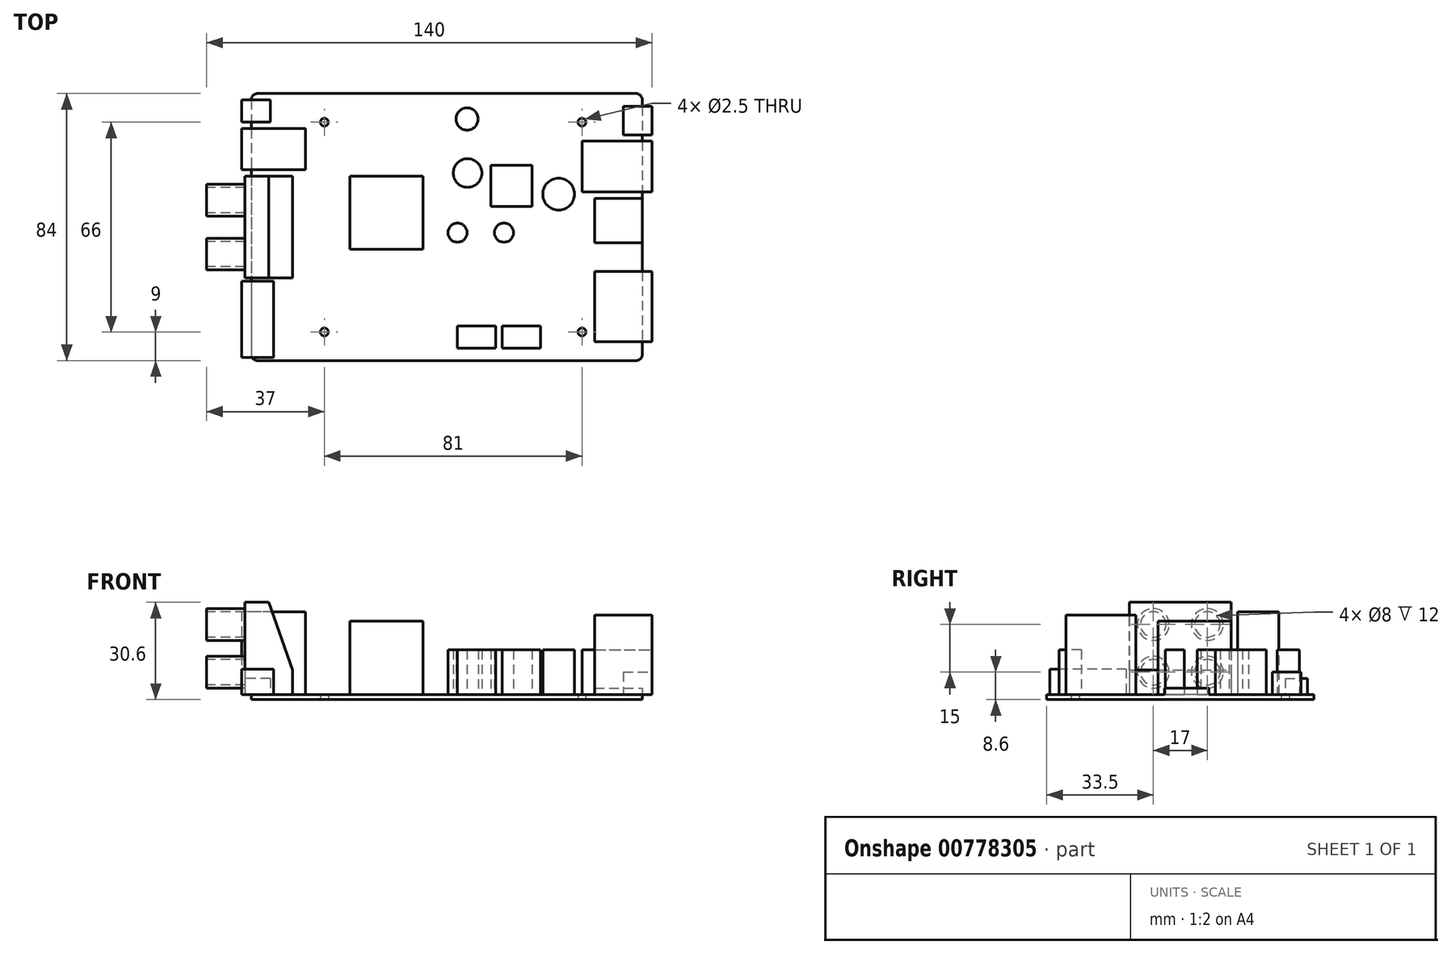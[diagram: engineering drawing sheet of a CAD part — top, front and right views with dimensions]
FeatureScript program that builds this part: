
annotation { "Feature Type Name" : "Feature", "Feature Type Description" : "" }
export const myFeature = defineFeature(function(context is Context, id is Id, definition is map)
    precondition{}
    {
        {
            var Q0;
            Q0=qCreatedBy(makeId("Top.planeOp"),FACE);
            var sketch = newSketch(context, id + "F0", { "sketchPlane" : qUnion([Q0])});
            skLineSegment(sketch, "E0.bottom", {"start": v(-40.5, 33) * mm, "end": v(40.5, 33) * mm, "construction": true});
            skLineSegment(sketch, "E0.top", {"start": v(-40.5, -33) * mm, "end": v(40.5, -33) * mm, "construction": true});
            skLineSegment(sketch, "E0.left", {"start": v(-40.5, 33) * mm, "end": v(-40.5, -33) * mm, "construction": true});
            skLineSegment(sketch, "E0.right", {"start": v(40.5, 33) * mm, "end": v(40.5, -33) * mm, "construction": true});
            skPoint(sketch, "E0.middle", {"position": v(0, 0) * mm});
            skCircle(sketch, "E1", {"center": v(-40.5, 33) * mm, "radius": 1.25 * mm});
            skCircle(sketch, "E2.0.1.0", {"center": v(-40.5, -33) * mm, "radius": 1.25 * mm});
            skCircle(sketch, "E2.1.0.0", {"center": v(40.5, 33) * mm, "radius": 1.25 * mm});
            skCircle(sketch, "E2.1.1.0", {"center": v(40.5, -33) * mm, "radius": 1.25 * mm});
            skLineSegment(sketch, "E3.bottom", {"start": v(-61.5, 42) * mm, "end": v(57.5, 42) * mm});
            skLineSegment(sketch, "E3.top", {"start": v(-61.5, -42) * mm, "end": v(57.5, -42) * mm});
            skLineSegment(sketch, "E3.left", {"start": v(-63.5, 40) * mm, "end": v(-63.5, -40) * mm});
            skLineSegment(sketch, "E3.right", {"start": v(59.5, 40) * mm, "end": v(59.5, -40) * mm});
            skPoint(sketch, "E3.middle", {"position": v(-2, 0) * mm});
            skPoint(sketch, "E4.visualSharp", {"position": v(-63.5, 42) * mm});
            skArc(sketch, "E4.filletArc", {"start": v(-61.5, 42) * mm, "mid": v(-62.91, 41.41) * mm, "end": v(-63.5, 40) * mm});
            skPoint(sketch, "E5.visualSharp", {"position": v(59.5, 42) * mm});
            skArc(sketch, "E5.filletArc", {"start": v(59.5, 40) * mm, "mid": v(58.91, 41.41) * mm, "end": v(57.5, 42) * mm});
            skPoint(sketch, "E6.visualSharp", {"position": v(59.5, -42) * mm});
            skArc(sketch, "E6.filletArc", {"start": v(57.5, -42) * mm, "mid": v(58.91, -41.41) * mm, "end": v(59.5, -40) * mm});
            skPoint(sketch, "E7.visualSharp", {"position": v(-63.5, -42) * mm});
            skArc(sketch, "E7.filletArc", {"start": v(-63.5, -40) * mm, "mid": v(-62.91, -41.41) * mm, "end": v(-61.5, -42) * mm});
            skSolve(sketch);
        }
        {
            var Q0;
            Q0=makeQuery(id+"F0.imprint","IMPRINT",FACE,{"disambiguationData":[TD([[makeQuery(id+"F0.imprint","IMPRINT",EDGE,{"derivedFrom":sQuery(id+"F0.wireOp",EDGE,"E1")}),-1.0]])]});
            extrude(context, id + "F1", {"entities" : qUnion([Q0]), "depth" : 1.6 * mm, "offsetDistance" : 25 * mm});
        }
        {
            var Q0;
            Q0=makeQuery(id+"F1.opExtrude","CAP_FACE",FACE,{"disambiguationData":[OSD([sQuery(id+"F0.wireOp",EDGE,"E1"),sQuery(id+"F0.wireOp",EDGE,"E2.0.1.0"),sQuery(id+"F0.wireOp",EDGE,"E2.1.0.0"),sQuery(id+"F0.wireOp",EDGE,"E2.1.1.0"),sQuery(id+"F0.wireOp",EDGE,"E3.bottom"),sQuery(id+"F0.wireOp",EDGE,"E3.top"),sQuery(id+"F0.wireOp",EDGE,"E3.left"),sQuery(id+"F0.wireOp",EDGE,"E3.right"),sQuery(id+"F0.wireOp",EDGE,"E4.filletArc"),sQuery(id+"F0.wireOp",EDGE,"E5.filletArc"),sQuery(id+"F0.wireOp",EDGE,"E6.filletArc"),sQuery(id+"F0.wireOp",EDGE,"E7.filletArc")])],"isStart":false});
            var sketch = newSketch(context, id + "F2", { "sketchPlane" : qUnion([Q0])});
            skLineSegment(sketch, "E8.bottom", {"start": v(-57.5, 33) * mm, "end": v(-66.5, 33) * mm});
            skLineSegment(sketch, "E8.top", {"start": v(-57.5, 40) * mm, "end": v(-66.5, 40) * mm});
            skLineSegment(sketch, "E8.left", {"start": v(-57.5, 33) * mm, "end": v(-57.5, 40) * mm});
            skLineSegment(sketch, "E8.right", {"start": v(-66.5, 33) * mm, "end": v(-66.5, 40) * mm});
            skPoint(sketch, "E8.middle", {"position": v(-62, 36.5) * mm});
            skLineSegment(sketch, "E9.bottom", {"start": v(-46.5, 18) * mm, "end": v(-66.5, 18) * mm});
            skLineSegment(sketch, "E9.top", {"start": v(-46.5, 31) * mm, "end": v(-66.5, 31) * mm});
            skLineSegment(sketch, "E9.left", {"start": v(-46.5, 18) * mm, "end": v(-46.5, 31) * mm});
            skLineSegment(sketch, "E9.right", {"start": v(-66.5, 18) * mm, "end": v(-66.5, 31) * mm});
            skPoint(sketch, "E9.middle", {"position": v(-56.5, 24.5) * mm});
            skLineSegment(sketch, "E10.bottom", {"start": v(-77.5, 16) * mm, "end": v(-50.5, 16) * mm});
            skLineSegment(sketch, "E10.top", {"start": v(-77.5, 0) * mm, "end": v(-50.5, 0) * mm});
            skLineSegment(sketch, "E10.left", {"start": v(-77.5, 16) * mm, "end": v(-77.5, 0) * mm});
            skLineSegment(sketch, "E10.right", {"start": v(-50.5, 16) * mm, "end": v(-50.5, 0) * mm});
            skPoint(sketch, "E10.middle", {"position": v(-64, 8) * mm});
            skLineSegment(sketch, "E11.bottom", {"start": v(-66.5, -17) * mm, "end": v(-56.5, -17) * mm});
            skLineSegment(sketch, "E11.top", {"start": v(-66.5, -41) * mm, "end": v(-56.5, -41) * mm});
            skLineSegment(sketch, "E11.left", {"start": v(-66.5, -17) * mm, "end": v(-66.5, -41) * mm});
            skLineSegment(sketch, "E11.right", {"start": v(-56.5, -17) * mm, "end": v(-56.5, -41) * mm});
            skPoint(sketch, "E11.middle", {"position": v(-61.5, -29) * mm});
            skLineSegment(sketch, "E12.bottom", {"start": v(53.5, 38) * mm, "end": v(62.5, 38) * mm});
            skLineSegment(sketch, "E12.top", {"start": v(53.5, 29) * mm, "end": v(62.5, 29) * mm});
            skLineSegment(sketch, "E12.left", {"start": v(53.5, 38) * mm, "end": v(53.5, 29) * mm});
            skLineSegment(sketch, "E12.right", {"start": v(62.5, 38) * mm, "end": v(62.5, 29) * mm});
            skPoint(sketch, "E12.middle", {"position": v(58, 33.5) * mm});
            skLineSegment(sketch, "E13.bottom", {"start": v(40.5, 27) * mm, "end": v(62.5, 27) * mm});
            skLineSegment(sketch, "E13.top", {"start": v(40.5, 11) * mm, "end": v(62.5, 11) * mm});
            skLineSegment(sketch, "E13.left", {"start": v(40.5, 27) * mm, "end": v(40.5, 11) * mm});
            skLineSegment(sketch, "E13.right", {"start": v(62.5, 27) * mm, "end": v(62.5, 11) * mm});
            skPoint(sketch, "E13.middle", {"position": v(51.5, 19) * mm});
            skLineSegment(sketch, "E14.bottom", {"start": v(44.5, 9) * mm, "end": v(59.5, 9) * mm});
            skLineSegment(sketch, "E14.top", {"start": v(44.5, -5) * mm, "end": v(59.5, -5) * mm});
            skLineSegment(sketch, "E14.left", {"start": v(44.5, 9) * mm, "end": v(44.5, -5) * mm});
            skLineSegment(sketch, "E14.right", {"start": v(59.5, 9) * mm, "end": v(59.5, -5) * mm});
            skPoint(sketch, "E14.middle", {"position": v(52, 2) * mm});
            skLineSegment(sketch, "E15.bottom", {"start": v(44.5, -14) * mm, "end": v(62.5, -14) * mm});
            skLineSegment(sketch, "E15.top", {"start": v(44.5, -36) * mm, "end": v(62.5, -36) * mm});
            skLineSegment(sketch, "E15.left", {"start": v(44.5, -14) * mm, "end": v(44.5, -36) * mm});
            skLineSegment(sketch, "E15.right", {"start": v(62.5, -14) * mm, "end": v(62.5, -36) * mm});
            skPoint(sketch, "E15.middle", {"position": v(53.5, -25) * mm});
            skLineSegment(sketch, "E16.MirrorCS", {"start": v(-50.5, -16) * mm, "end": v(-50.5, 0) * mm});
            skLineSegment(sketch, "E17.MirrorCS", {"start": v(-77.5, -16) * mm, "end": v(-77.5, 0) * mm});
            skLineSegment(sketch, "E18.MirrorCS", {"start": v(-77.5, -16) * mm, "end": v(-50.5, -16) * mm});
            skLineSegment(sketch, "E19.bottom", {"start": v(-32.5, 16) * mm, "end": v(-9.5, 16) * mm});
            skLineSegment(sketch, "E19.top", {"start": v(-32.5, -7) * mm, "end": v(-9.5, -7) * mm});
            skLineSegment(sketch, "E19.left", {"start": v(-32.5, 16) * mm, "end": v(-32.5, -7) * mm});
            skLineSegment(sketch, "E19.right", {"start": v(-9.5, 16) * mm, "end": v(-9.5, -7) * mm});
            skPoint(sketch, "E19.middle", {"position": v(-21, 4.5) * mm});
            skCircle(sketch, "E20", {"center": v(4.37, 34) * mm, "radius": 3.5 * mm});
            skCircle(sketch, "E21", {"center": v(4.52, 17) * mm, "radius": 4.5 * mm});
            skCircle(sketch, "E22", {"center": v(1.37, -1.76) * mm, "radius": 3 * mm});
            skCircle(sketch, "E23", {"center": v(15.98, -1.76) * mm, "radius": 3 * mm});
            skLineSegment(sketch, "E24.bottom", {"start": v(11.84, 19.5) * mm, "end": v(24.84, 19.5) * mm});
            skLineSegment(sketch, "E24.top", {"start": v(11.84, 6.5) * mm, "end": v(24.84, 6.5) * mm});
            skLineSegment(sketch, "E24.left", {"start": v(11.84, 19.5) * mm, "end": v(11.84, 6.5) * mm});
            skLineSegment(sketch, "E24.right", {"start": v(24.84, 19.5) * mm, "end": v(24.84, 6.5) * mm});
            skPoint(sketch, "E24.middle", {"position": v(18.34, 13) * mm});
            skCircle(sketch, "E25", {"center": v(33.18, 10.36) * mm, "radius": 5 * mm});
            skLineSegment(sketch, "E26.bottom", {"start": v(1.37, -31.15) * mm, "end": v(13.37, -31.15) * mm});
            skLineSegment(sketch, "E26.top", {"start": v(1.37, -38.15) * mm, "end": v(13.37, -38.15) * mm});
            skLineSegment(sketch, "E26.left", {"start": v(1.37, -31.15) * mm, "end": v(1.37, -38.15) * mm});
            skLineSegment(sketch, "E26.right", {"start": v(13.37, -31.15) * mm, "end": v(13.37, -38.15) * mm});
            skLineSegment(sketch, "E27.bottom", {"start": v(15.47, -31.15) * mm, "end": v(27.47, -31.15) * mm});
            skLineSegment(sketch, "E27.top", {"start": v(15.47, -38.15) * mm, "end": v(27.47, -38.15) * mm});
            skLineSegment(sketch, "E27.left", {"start": v(15.47, -31.15) * mm, "end": v(15.47, -38.15) * mm});
            skLineSegment(sketch, "E27.right", {"start": v(27.47, -31.15) * mm, "end": v(27.47, -38.15) * mm});
            skSolve(sketch);
        }
        {
            var Q0;
            {var subQ0=sQuery(id+"F2.wireOp",EDGE,"E8.right");Q0=makeQuery(id+"F2.imprint","IMPRINT",FACE,{"disambiguationData":[TD([[makeQuery(id+"F2.imprint","IMPRINT",EDGE,{"derivedFrom":subQ0}),-1.0]])]});}
            var Q1;
            {var subQ0=sQuery(id+"F2.wireOp",EDGE,"E8.left");Q1=makeQuery(id+"F2.imprint","IMPRINT",FACE,{"disambiguationData":[TD([[makeQuery(id+"F2.imprint","IMPRINT",EDGE,{"derivedFrom":subQ0}),1.0]])]});}
            extrude(context, id + "F3", {"entities" : qUnion([Q0, Q1]), "operationType" : NewBodyOperationType.ADD, "depth" : 5 * mm, "offsetDistance" : 25 * mm});
        }
        {
            var Q0;
            {var subQ5=sQuery(id+"F2.wireOp",EDGE,"E11.right");Q0=makeQuery(id+"F2.imprint","IMPRINT",FACE,{"disambiguationData":[TD([[makeQuery(id+"F2.imprint","IMPRINT",EDGE,{"derivedFrom":subQ5}),-1.0]])]});}
            var Q1;
            {var subQ5=sQuery(id+"F2.wireOp",EDGE,"E11.left");Q1=makeQuery(id+"F2.imprint","IMPRINT",FACE,{"disambiguationData":[TD([[makeQuery(id+"F2.imprint","IMPRINT",EDGE,{"derivedFrom":subQ5}),1.0]])]});}
            extrude(context, id + "F4", {"entities" : qUnion([Q0, Q1]), "operationType" : NewBodyOperationType.ADD, "depth" : 8 * mm, "offsetDistance" : 25 * mm});
        }
        {
            var Q0;
            {var subQ0=sQuery(id+"F2.wireOp",EDGE,"E10.left");Q0=makeQuery(id+"F2.imprint","IMPRINT",FACE,{"disambiguationData":[TD([[makeQuery(id+"F2.imprint","IMPRINT",EDGE,{"derivedFrom":subQ0}),1.0]])]});}
            var Q1;
            {var subQ0=sQuery(id+"F2.wireOp",EDGE,"E10.right");Q1=makeQuery(id+"F2.imprint","IMPRINT",FACE,{"disambiguationData":[TD([[makeQuery(id+"F2.imprint","IMPRINT",EDGE,{"derivedFrom":subQ0}),-1.0]])]});}
            var Q2;
            {var subQ0=sQuery(id+"F2.wireOp",EDGE,"E17.MirrorCS");Q2=makeQuery(id+"F2.imprint","IMPRINT",FACE,{"disambiguationData":[TD([[makeQuery(id+"F2.imprint","IMPRINT",EDGE,{"derivedFrom":subQ0}),-1.0]])]});}
            var Q3;
            {var subQ0=sQuery(id+"F2.wireOp",EDGE,"E16.MirrorCS");Q3=makeQuery(id+"F2.imprint","IMPRINT",FACE,{"disambiguationData":[TD([[makeQuery(id+"F2.imprint","IMPRINT",EDGE,{"derivedFrom":subQ0}),1.0]])]});}
            extrude(context, id + "F5", {"entities" : qUnion([Q0, Q1, Q2, Q3]), "operationType" : NewBodyOperationType.ADD, "depth" : 29 * mm, "offsetDistance" : 25 * mm});
        }
        {
            var Q0;
            Q0=makeQuery(id+"F5.opExtrude","SWEPT_FACE",FACE,{"disambiguationData":[OSD([sQuery(id+"F2.wireOp",EDGE,"E10.left"),sQuery(id+"F2.wireOp",EDGE,"E17.MirrorCS")])]});
            var sketch = newSketch(context, id + "F6", { "sketchPlane" : qUnion([Q0])});
            skLineSegment(sketch, "E28.bottom", {"start": v(-8.5, 8.6) * mm, "end": v(8.5, 8.6) * mm, "construction": true});
            skLineSegment(sketch, "E28.top", {"start": v(-8.5, 23.6) * mm, "end": v(8.5, 23.6) * mm, "construction": true});
            skLineSegment(sketch, "E28.left", {"start": v(-8.5, 8.6) * mm, "end": v(-8.5, 23.6) * mm, "construction": true});
            skLineSegment(sketch, "E28.right", {"start": v(8.5, 8.6) * mm, "end": v(8.5, 23.6) * mm, "construction": true});
            skPoint(sketch, "E28.middle", {"position": v(0, 16.1) * mm});
            skPoint(sketch, "E28.middle.positionSnap0", {"position": v(-16, 16.1) * mm});
            skPoint(sketch, "E28.centerSnap0", {"position": v(-16, 16.1) * mm});
            skCircle(sketch, "E29", {"center": v(-8.5, 23.6) * mm, "radius": 5 * mm});
            skCircle(sketch, "E30.0.1.0", {"center": v(-8.5, 8.6) * mm, "radius": 5 * mm});
            skCircle(sketch, "E30.1.0.0", {"center": v(8.5, 23.6) * mm, "radius": 5 * mm});
            skCircle(sketch, "E30.1.1.0", {"center": v(8.5, 8.6) * mm, "radius": 5 * mm});
            skLineSegment(sketch, "E30.direction2", {"start": v(-8.5, 23.6) * mm, "end": v(-8.5, 8.6) * mm, "construction": true});
            skCircle(sketch, "E31", {"center": v(-8.5, 23.6) * mm, "radius": 4 * mm});
            skCircle(sketch, "E32.0.1.0", {"center": v(-8.5, 8.6) * mm, "radius": 4 * mm});
            skCircle(sketch, "E32.1.0.0", {"center": v(8.5, 23.6) * mm, "radius": 4 * mm});
            skCircle(sketch, "E32.1.1.0", {"center": v(8.5, 8.6) * mm, "radius": 4 * mm});
            skSolve(sketch);
        }
        {
            var Q0;
            Q0=makeQuery(id+"F6.imprint","IMPRINT",FACE,{"disambiguationData":[TD([[makeQuery(id+"F6.imprint","IMPRINT",EDGE,{"derivedFrom":sQuery(id+"F6.wireOp",EDGE,"E29")}),-1.0]])]});
            var Q1;
            Q1=makeQuery(id+"F6.imprint","IMPRINT",FACE,{"disambiguationData":[TD([[makeQuery(id+"F6.imprint","IMPRINT",EDGE,{"derivedFrom":sQuery(id+"F6.wireOp",EDGE,"E31")}),1.0]])]});
            var Q2;
            Q2=makeQuery(id+"F6.imprint","IMPRINT",FACE,{"disambiguationData":[TD([[makeQuery(id+"F6.imprint","IMPRINT",EDGE,{"derivedFrom":sQuery(id+"F6.wireOp",EDGE,"E32.1.0.0")}),1.0]])]});
            var Q3;
            Q3=makeQuery(id+"F6.imprint","IMPRINT",FACE,{"disambiguationData":[TD([[makeQuery(id+"F6.imprint","IMPRINT",EDGE,{"derivedFrom":sQuery(id+"F6.wireOp",EDGE,"E32.0.1.0")}),1.0]])]});
            var Q4;
            Q4=makeQuery(id+"F6.imprint","IMPRINT",FACE,{"disambiguationData":[TD([[makeQuery(id+"F6.imprint","IMPRINT",EDGE,{"derivedFrom":sQuery(id+"F6.wireOp",EDGE,"E32.1.1.0")}),1.0]])]});
            extrude(context, id + "F7", {"entities" : qUnion([Q0, Q1, Q2, Q3, Q4]), "operationType" : NewBodyOperationType.REMOVE, "oppositeDirection" : true, "depth" : 12 * mm, "offsetDistance" : 25 * mm});
        }
        {
            var Q0;
            Q0=makeQuery(id+"F5.opExtrude","SWEPT_FACE",FACE,{"disambiguationData":[OSD([sQuery(id+"F2.wireOp",EDGE,"E10.bottom")])]});
            var sketch = newSketch(context, id + "F8", { "sketchPlane" : qUnion([Q0])});
            skLineSegment(sketch, "E33", {"start": v(58, 30.6) * mm, "end": v(50.5, 9.32) * mm});
            skSolve(sketch);
        }
        {
            var Q0;
            {var subQ0=sQuery(id+"F8.wireOp",EDGE,"E33");Q0=makeQuery(id+"F8.imprint","IMPRINT",FACE,{"disambiguationData":[TD([[makeQuery(id+"F8.imprint","IMPRINT",EDGE,{"derivedFrom":subQ0}),-1.0]])]});}
            extrude(context, id + "F9", {"entities" : qUnion([Q0]), "operationType" : NewBodyOperationType.REMOVE, "endBound" : BoundingType.UP_TO_NEXT, "oppositeDirection" : true, "depth" : 25 * mm, "offsetDistance" : 25 * mm});
        }
        {
            var Q0;
            {var subQ0=sQuery(id+"F2.wireOp",EDGE,"E9.right");Q0=makeQuery(id+"F2.imprint","IMPRINT",FACE,{"disambiguationData":[TD([[makeQuery(id+"F2.imprint","IMPRINT",EDGE,{"derivedFrom":subQ0}),-1.0]])]});}
            var Q1;
            {var subQ0=sQuery(id+"F2.wireOp",EDGE,"E9.left");Q1=makeQuery(id+"F2.imprint","IMPRINT",FACE,{"disambiguationData":[TD([[makeQuery(id+"F2.imprint","IMPRINT",EDGE,{"derivedFrom":subQ0}),1.0]])]});}
            extrude(context, id + "F10", {"entities" : qUnion([Q0, Q1]), "operationType" : NewBodyOperationType.ADD, "depth" : 26 * mm, "offsetDistance" : 25 * mm});
        }
        {
            var Q0;
            {var subQ0=sQuery(id+"F2.wireOp",EDGE,"E12.left");Q0=makeQuery(id+"F2.imprint","IMPRINT",FACE,{"disambiguationData":[TD([[makeQuery(id+"F2.imprint","IMPRINT",EDGE,{"derivedFrom":subQ0}),1.0]])]});}
            var Q1;
            {var subQ0=sQuery(id+"F2.wireOp",EDGE,"E12.right");Q1=makeQuery(id+"F2.imprint","IMPRINT",FACE,{"disambiguationData":[TD([[makeQuery(id+"F2.imprint","IMPRINT",EDGE,{"derivedFrom":subQ0}),-1.0]])]});}
            extrude(context, id + "F11", {"entities" : qUnion([Q0, Q1]), "operationType" : NewBodyOperationType.ADD, "depth" : 7 * mm, "offsetDistance" : 25 * mm});
        }
        {
            var Q0;
            {var subQ0=sQuery(id+"F2.wireOp",EDGE,"E13.left");Q0=makeQuery(id+"F2.imprint","IMPRINT",FACE,{"disambiguationData":[TD([[makeQuery(id+"F2.imprint","IMPRINT",EDGE,{"derivedFrom":subQ0}),1.0]])]});}
            var Q1;
            {var subQ0=sQuery(id+"F2.wireOp",EDGE,"E13.right");Q1=makeQuery(id+"F2.imprint","IMPRINT",FACE,{"disambiguationData":[TD([[makeQuery(id+"F2.imprint","IMPRINT",EDGE,{"derivedFrom":subQ0}),-1.0]])]});}
            var Q2;
            Q2=makeQuery(id+"F2.imprint","IMPRINT",FACE,{"disambiguationData":[TD([[makeQuery(id+"F2.imprint","IMPRINT",EDGE,{"derivedFrom":sQuery(id+"F2.wireOp",EDGE,"E20")}),1.0]])]});
            var Q3;
            Q3=makeQuery(id+"F2.imprint","IMPRINT",FACE,{"disambiguationData":[TD([[makeQuery(id+"F2.imprint","IMPRINT",EDGE,{"derivedFrom":sQuery(id+"F2.wireOp",EDGE,"E21")}),1.0]])]});
            var Q4;
            Q4=makeQuery(id+"F2.imprint","IMPRINT",FACE,{"disambiguationData":[TD([[makeQuery(id+"F2.imprint","IMPRINT",EDGE,{"derivedFrom":sQuery(id+"F2.wireOp",EDGE,"E24.bottom")}),-1.0]])]});
            var Q5;
            Q5=makeQuery(id+"F2.imprint","IMPRINT",FACE,{"disambiguationData":[TD([[makeQuery(id+"F2.imprint","IMPRINT",EDGE,{"derivedFrom":sQuery(id+"F2.wireOp",EDGE,"E25")}),1.0]])]});
            var Q6;
            Q6=makeQuery(id+"F2.imprint","IMPRINT",FACE,{"disambiguationData":[TD([[makeQuery(id+"F2.imprint","IMPRINT",EDGE,{"derivedFrom":sQuery(id+"F2.wireOp",EDGE,"E23")}),1.0]])]});
            var Q7;
            Q7=makeQuery(id+"F2.imprint","IMPRINT",FACE,{"disambiguationData":[TD([[makeQuery(id+"F2.imprint","IMPRINT",EDGE,{"derivedFrom":sQuery(id+"F2.wireOp",EDGE,"E22")}),1.0]])]});
            var Q8;
            Q8=makeQuery(id+"F2.imprint","IMPRINT",FACE,{"disambiguationData":[TD([[makeQuery(id+"F2.imprint","IMPRINT",EDGE,{"derivedFrom":sQuery(id+"F2.wireOp",EDGE,"E26.bottom")}),-1.0]])]});
            var Q9;
            Q9=makeQuery(id+"F2.imprint","IMPRINT",FACE,{"disambiguationData":[TD([[makeQuery(id+"F2.imprint","IMPRINT",EDGE,{"derivedFrom":sQuery(id+"F2.wireOp",EDGE,"E27.bottom")}),-1.0]])]});
            extrude(context, id + "F12", {"entities" : qUnion([Q0, Q1, Q2, Q3, Q4, Q5, Q6, Q7, Q8, Q9]), "operationType" : NewBodyOperationType.ADD, "depth" : 14 * mm, "offsetDistance" : 25 * mm});
        }
        {
            var Q0;
            Q0=makeQuery(id+"F2.imprint","IMPRINT",FACE,{"disambiguationData":[TD([[makeQuery(id+"F2.imprint","IMPRINT",EDGE,{"derivedFrom":sQuery(id+"F2.wireOp",EDGE,"E14.bottom")}),-1.0]])]});
            extrude(context, id + "F13", {"entities" : qUnion([Q0]), "operationType" : NewBodyOperationType.ADD, "depth" : 2 * mm, "offsetDistance" : 25 * mm});
        }
        {
            var Q0;
            {var subQ0=sQuery(id+"F2.wireOp",EDGE,"E15.left");Q0=makeQuery(id+"F2.imprint","IMPRINT",FACE,{"disambiguationData":[TD([[makeQuery(id+"F2.imprint","IMPRINT",EDGE,{"derivedFrom":subQ0}),1.0]])]});}
            var Q1;
            {var subQ0=sQuery(id+"F2.wireOp",EDGE,"E15.right");Q1=makeQuery(id+"F2.imprint","IMPRINT",FACE,{"disambiguationData":[TD([[makeQuery(id+"F2.imprint","IMPRINT",EDGE,{"derivedFrom":subQ0}),-1.0]])]});}
            extrude(context, id + "F14", {"entities" : qUnion([Q0, Q1]), "operationType" : NewBodyOperationType.ADD, "depth" : 25 * mm, "offsetDistance" : 25 * mm});
        }
        {
            var Q0;
            Q0=makeQuery(id+"F2.imprint","IMPRINT",FACE,{"disambiguationData":[TD([[makeQuery(id+"F2.imprint","IMPRINT",EDGE,{"derivedFrom":sQuery(id+"F2.wireOp",EDGE,"E19.bottom")}),-1.0]])]});
            extrude(context, id + "F15", {"entities" : qUnion([Q0]), "operationType" : NewBodyOperationType.ADD, "depth" : 23 * mm, "offsetDistance" : 25 * mm});
        }
    });
